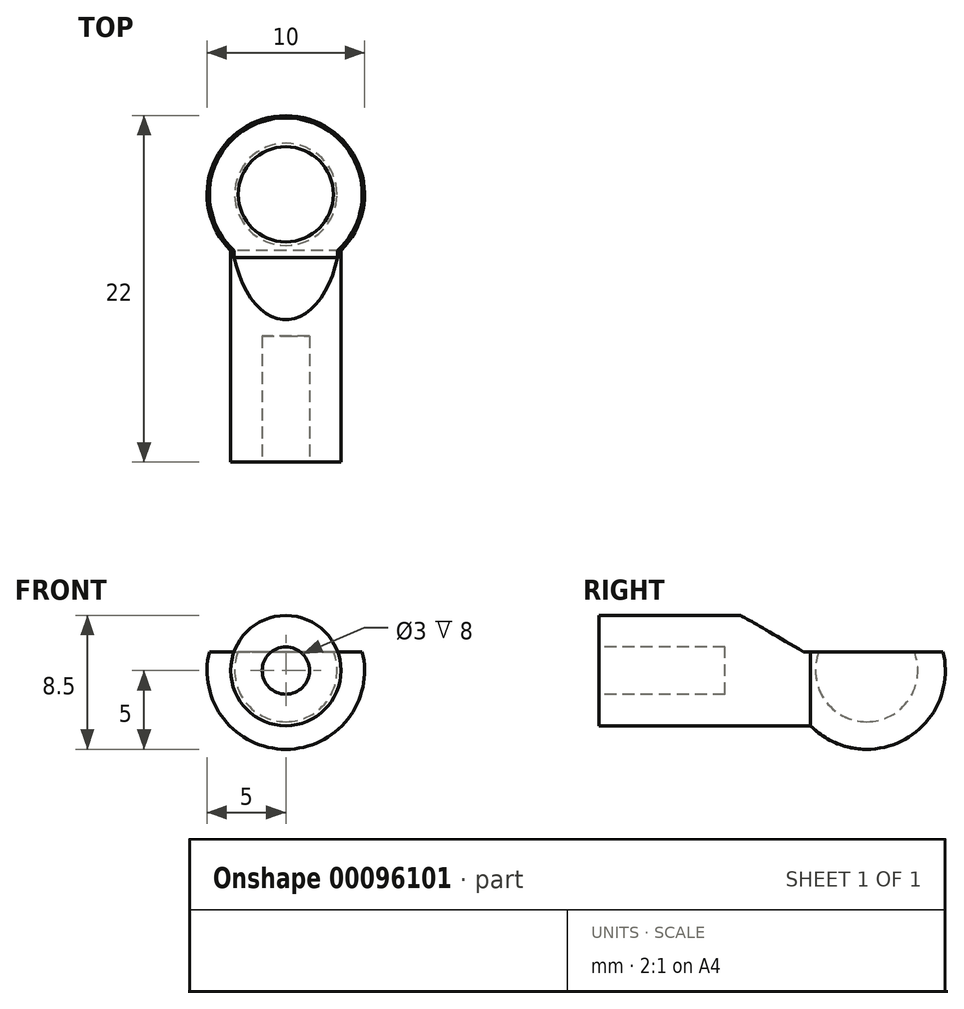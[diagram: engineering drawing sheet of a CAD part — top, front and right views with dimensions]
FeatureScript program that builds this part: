
annotation { "Feature Type Name" : "Feature", "Feature Type Description" : "" }
export const myFeature = defineFeature(function(context is Context, id is Id, definition is map)
    precondition{}
    {
        {
            var Q0;
            Q0=qCreatedBy(makeId("Right.planeOp"),FACE);
            var sketch = newSketch(context, id + "F0", { "sketchPlane" : qUnion([Q0])});
            skArc(sketch, "E0", {"start": v(0, -5) * mm, "mid": v(5, 0) * mm, "end": v(0, 5) * mm});
            skLineSegment(sketch, "E1", {"start": v(0, 5) * mm, "end": v(0, -5) * mm});
            skSolve(sketch);
        }
        {
            var Q0;
            Q0 = qSketchRegion(id + "F0", true);
            var Q1;
            Q1=sQuery(id+"F0.wireOp",EDGE,"E1");
            revolve(context, id + "F1", {"entities" : qUnion([Q0]), "axis" : qUnion([Q1]), "revolveType" : RevolveType.FULL});
        }
        {
            var Q0;
            Q0=qCreatedBy(makeId("Front.planeOp"),FACE);
            var sketch = newSketch(context, id + "F2", { "sketchPlane" : qUnion([Q0])});
            skCircle(sketch, "E2", {"center": v(0, 0) * mm, "radius": 3.5 * mm});
            skSolve(sketch);
        }
        {
            var Q0;
            Q0 = qSketchRegion(id + "F2", true);
            extrude(context, id + "F3", {"entities" : qUnion([Q0]), "operationType" : NewBodyOperationType.ADD, "depth" : 17 * mm});
        }
        {
            var Q0;
            Q0=qCreatedBy(makeId("Right.planeOp"),FACE);
            var sketch = newSketch(context, id + "F4", { "sketchPlane" : qUnion([Q0])});
            skArc(sketch, "E3", {"start": v(0, -3.25) * mm, "mid": v(3.25, 0) * mm, "end": v(0, 3.25) * mm});
            skLineSegment(sketch, "E4", {"start": v(0, 3.25) * mm, "end": v(0, -3.25) * mm});
            skSolve(sketch);
        }
        {
            var Q0;
            Q0 = qSketchRegion(id + "F4", true);
            var Q1;
            Q1=sQuery(id+"F4.wireOp",EDGE,"E4");
            revolve(context, id + "F5", {"operationType" : NewBodyOperationType.REMOVE, "entities" : qUnion([Q0]), "axis" : qUnion([Q1]), "revolveType" : RevolveType.FULL, "oppositeDirection" : true});
        }
        {
            var Q0;
            Q0=qCreatedBy(makeId("Right.planeOp"),FACE);
            var sketch = newSketch(context, id + "F6", { "sketchPlane" : qUnion([Q0])});
            skLineSegment(sketch, "E5", {"start": v(5.5, 1.2) * mm, "end": v(-4, 1.2) * mm});
            skLineSegment(sketch, "E6", {"start": v(-4, 1.2) * mm, "end": v(-10.93, 5.2) * mm});
            skLineSegment(sketch, "E7", {"start": v(-10.93, 5.2) * mm, "end": v(5.5, 5.2) * mm});
            skLineSegment(sketch, "E8", {"start": v(5.5, 5.2) * mm, "end": v(5.5, 1.2) * mm});
            skSolve(sketch);
        }
        {
            var Q0;
            Q0 = qSketchRegion(id + "F6", true);
            extrude(context, id + "F7", {"entities" : qUnion([Q0]), "operationType" : NewBodyOperationType.REMOVE, "oppositeDirection" : true, "depth" : 6 * mm, "hasSecondDirection" : true, "secondDirectionOppositeDirection" : false, "secondDirectionDepth" : 6 * mm});
        }
        {
            var Q0;
            Q0=makeQuery(id+"F3.opExtrude","CAP_FACE",FACE,{"disambiguationData":[OSD([sQuery(id+"F2.wireOp",EDGE,"E2")])],"isStart":false});
            var sketch = newSketch(context, id + "F8", { "sketchPlane" : qUnion([Q0])});
            skCircle(sketch, "E9", {"center": v(0, 0) * mm, "radius": 1.5 * mm});
            skSolve(sketch);
        }
        {
            var Q0;
            Q0 = qSketchRegion(id + "F8", true);
            extrude(context, id + "F9", {"entities" : qUnion([Q0]), "operationType" : NewBodyOperationType.REMOVE, "oppositeDirection" : true, "depth" : 8 * mm});
        }
    });
